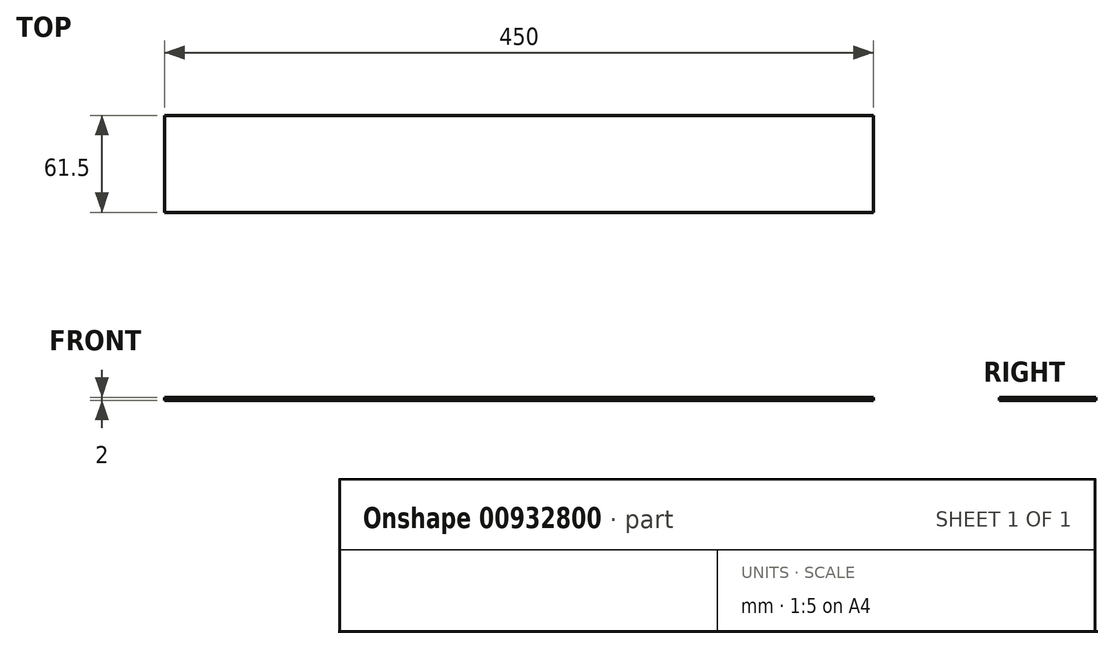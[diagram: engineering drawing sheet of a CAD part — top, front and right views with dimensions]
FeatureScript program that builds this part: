
annotation { "Feature Type Name" : "Feature", "Feature Type Description" : "" }
export const myFeature = defineFeature(function(context is Context, id is Id, definition is map)
    precondition{}
    {
        {
            var Q0;
            Q0=qCreatedBy(makeId("Top.planeOp"),FACE);
            var sketch = newSketch(context, id + "F0", { "sketchPlane" : qUnion([Q0])});
            skLineSegment(sketch, "E0.bottom", {"start": v(0, 0) * mm, "end": v(450, 0) * mm});
            skLineSegment(sketch, "E0.top", {"start": v(0, 61.5) * mm, "end": v(450, 61.5) * mm});
            skLineSegment(sketch, "E0.left", {"start": v(0, 0) * mm, "end": v(0, 61.5) * mm});
            skLineSegment(sketch, "E0.right", {"start": v(450, 0) * mm, "end": v(450, 61.5) * mm});
            skSolve(sketch);
        }
        {
            var Q0;
            Q0 = qSketchRegion(id + "F0", true);
            extrude(context, id + "F1", {"entities" : qUnion([Q0]), "depth" : 2 * mm, "offsetDistance" : 25 * mm});
        }
    });
